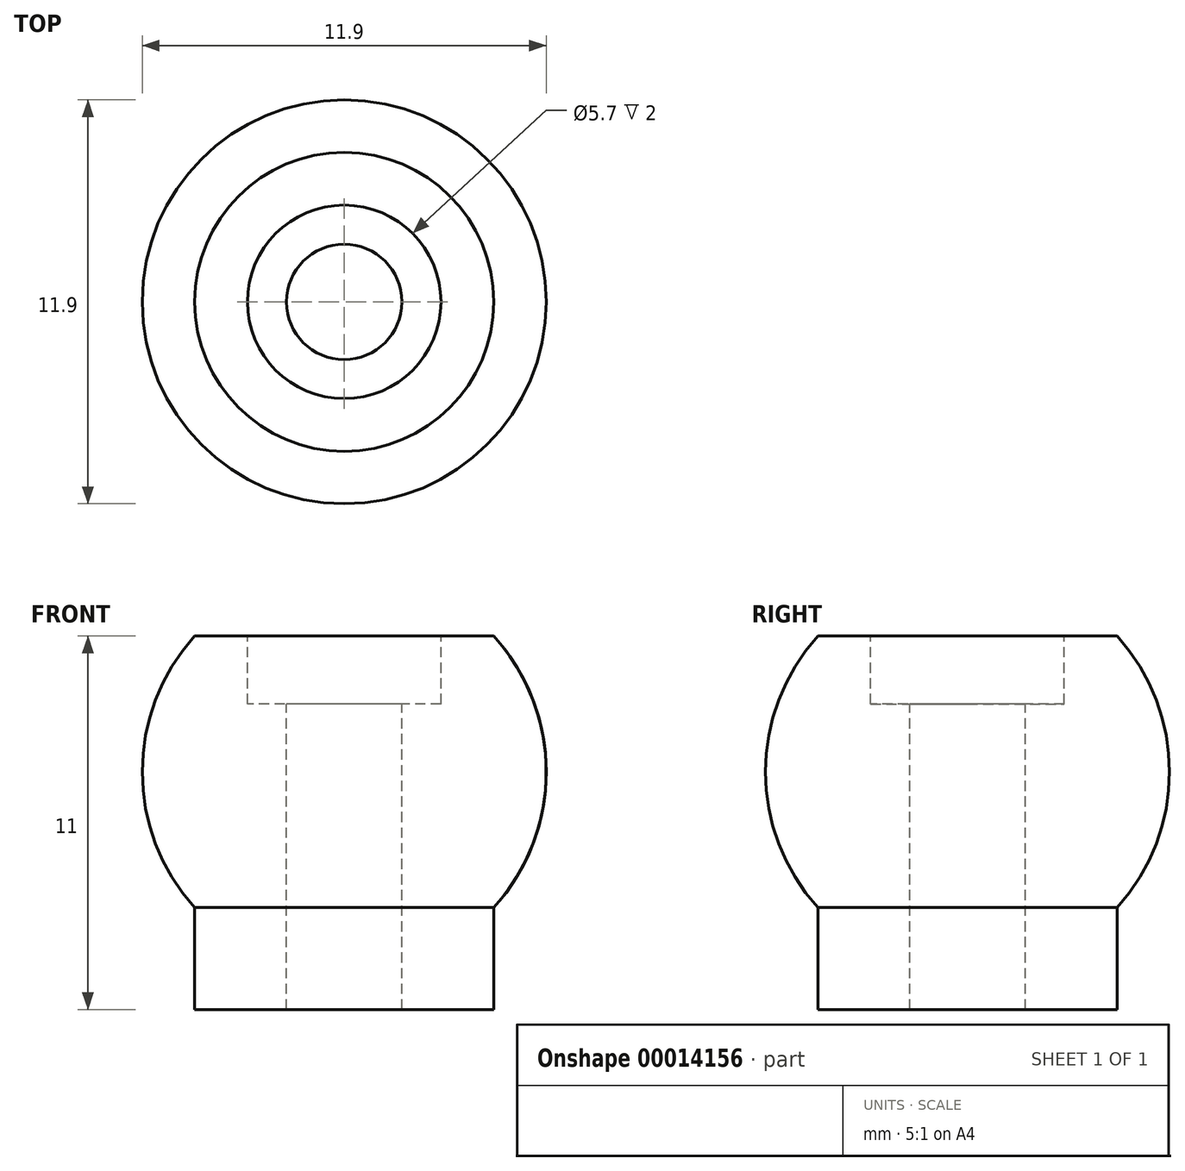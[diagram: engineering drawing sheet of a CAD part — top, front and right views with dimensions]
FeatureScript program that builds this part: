
annotation { "Feature Type Name" : "Feature", "Feature Type Description" : "" }
export const myFeature = defineFeature(function(context is Context, id is Id, definition is map)
    precondition{}
    {
        {
            var Q0;
            Q0=qCreatedBy(makeId("Front.planeOp"),FACE);
            var sketch = newSketch(context, id + "F0", { "sketchPlane" : qUnion([Q0])});
            skArc(sketch, "E0", {"start": v(4.4, -4) * mm, "mid": v(5.95, 0) * mm, "end": v(4.4, 4) * mm});
            skLineSegment(sketch, "E1", {"start": v(-9.99, 0) * mm, "end": v(11.52, 0) * mm, "construction": true});
            skLineSegment(sketch, "E2", {"start": v(0, 12.04) * mm, "end": v(0, -12.64) * mm, "construction": true});
            skLineSegment(sketch, "E3", {"start": v(0, 4) * mm, "end": v(4.4, 4) * mm});
            skLineSegment(sketch, "E4.0.MirrorCS", {"start": v(0, -4) * mm, "end": v(4.4, -4) * mm});
            skPoint(sketch, "E5.orphan", {"position": v(7.02, 4) * mm});
            skPoint(sketch, "E6.orphan", {"position": v(7.02, -4) * mm});
            skLineSegment(sketch, "E7", {"start": v(0, -4) * mm, "end": v(0, 4) * mm});
            skSolve(sketch);
        }
        {
            var Q0;
            Q0=makeQuery(id+"F0.imprint","IMPRINT",FACE,{"disambiguationData":[TD([[makeQuery(id+"F0.imprint","IMPRINT",EDGE,{"derivedFrom":sQuery(id+"F0.wireOp",EDGE,"E0")}),1.0]])]});
            var Q1;
            Q1=sQuery(id+"F0.wireOp",EDGE,"E2");
            revolve(context, id + "F1", {"entities" : qUnion([Q0]), "axis" : qUnion([Q1]), "revolveType" : RevolveType.FULL});
        }
        {
            var Q0;
            Q0=makeQuery(id+"F1.opRevolve","SWEPT_FACE",FACE,{"disambiguationData":[OSD([sQuery(id+"F0.wireOp",EDGE,"E4.0.MirrorCS")])]});
            extrude(context, id + "F2", {"entities" : qUnion([Q0]), "operationType" : NewBodyOperationType.ADD, "depth" : 3 * mm});
        }
        {
            var Q0;
            Q0=makeQuery(id+"F1.opRevolve","SWEPT_FACE",FACE,{"disambiguationData":[OSD([sQuery(id+"F0.wireOp",EDGE,"E3")])]});
            var sketch = newSketch(context, id + "F3", { "sketchPlane" : qUnion([Q0])});
            skCircle(sketch, "E8", {"center": v(0, 0) * mm, "radius": 1.7 * mm});
            skCircle(sketch, "E9", {"center": v(0, 0) * mm, "radius": 2.85 * mm});
            skSolve(sketch);
        }
        {
            var Q0;
            Q0=makeQuery(id+"F3.imprint","IMPRINT",FACE,{"disambiguationData":[TD([[makeQuery(id+"F3.imprint","IMPRINT",EDGE,{"derivedFrom":sQuery(id+"F3.wireOp",EDGE,"E8")}),1.0]])]});
            extrude(context, id + "F4", {"entities" : qUnion([Q0]), "operationType" : NewBodyOperationType.REMOVE, "endBound" : BoundingType.THROUGH_ALL, "oppositeDirection" : true, "depth" : 25 * mm});
        }
        {
            var Q0;
            Q0=makeQuery(id+"F3.imprint","IMPRINT",FACE,{"disambiguationData":[TD([[makeQuery(id+"F3.imprint","IMPRINT",EDGE,{"derivedFrom":sQuery(id+"F3.wireOp",EDGE,"E8")}),-1.0]])]});
            var Q1;
            Q1=sQuery(id+"F3.wireOp",EDGE,"E9");
            extrude(context, id + "F5", {"entities" : qUnion([Q0]), "operationType" : NewBodyOperationType.REMOVE, "surfaceEntities" : qUnion([Q1]), "oppositeDirection" : true, "depth" : 2 * mm});
        }
    });
